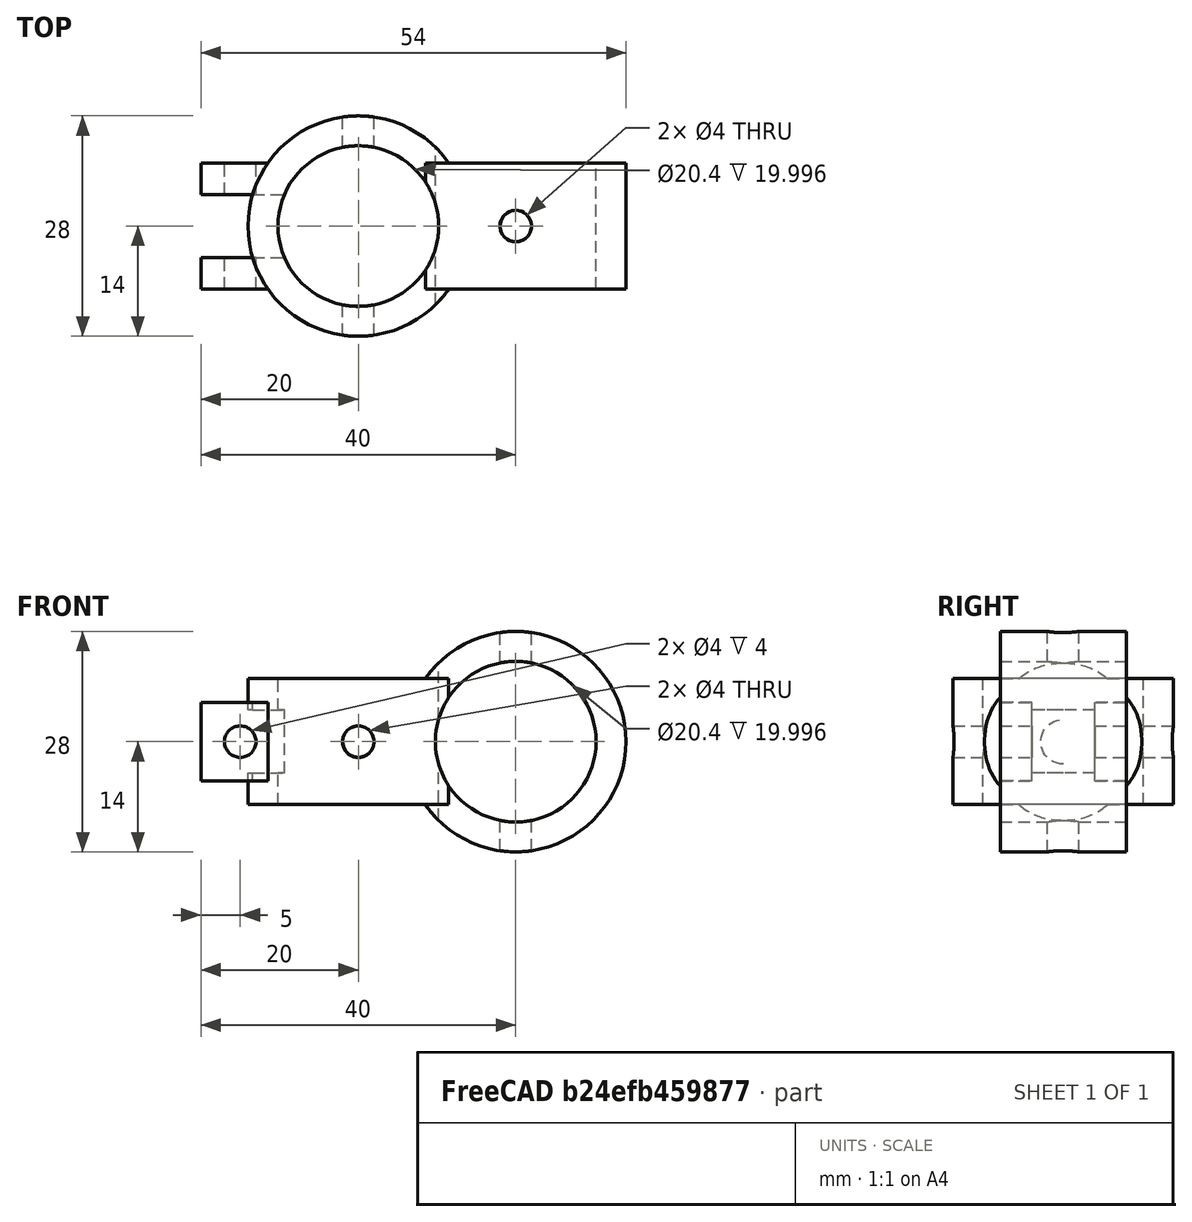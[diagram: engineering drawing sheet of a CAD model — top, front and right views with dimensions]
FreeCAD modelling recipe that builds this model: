
FCSTD DOCUMENT  (FreeCAD 0.17R13522 (Git))
Label: connector-rack-sleeper
License: All rights reserved
LicenseURL: http://en.wikipedia.org/wiki/All_rights_reserved
objects: Part::Cylinder×7, Part::Box×3, Part::MultiFuse×2, Part::Cut×1
note: 13 computed .brp shape members not serialized (recipe doc carries the construction recipe); baked Part::Feature solids carry a one-line shape summary decoded from their .brp

FEATURE [Part::Cylinder] Cylinder002
  Angle = 360
  AttacherType = Attacher::AttachEngine3D
  Height = 28
  Placement = pos=(-10,0,-10) rot=(0,0,1;0rad)
  Radius = 10.2
FEATURE [Part::Box] Box  label="Cube"
  AttacherType = Attacher::AttachEngine3D
  Height = 10
  Length = 10
  Placement = pos=(-30,-8,-5) rot=(0,0,1;0rad)
  Width = 4
FEATURE [Part::Cylinder] Cylinder004
  Angle = 360
  AttacherType = Attacher::AttachEngine3D
  Height = 16
  Placement = pos=(-25,-8,0) rot=(-1,0,0;1.5708rad)
  Radius = 2
FEATURE [Part::Cylinder] Cylinder
  Angle = 360
  AttacherType = Attacher::AttachEngine3D
  Height = 16
  Placement = pos=(-10,0,-8) rot=(0,0,1;0rad)
  Radius = 14
FEATURE [Part::Box] Box001  label="Cube001"
  AttacherType = Attacher::AttachEngine3D
  Height = 8
  Length = 5
  Placement = pos=(-24,-4,-4) rot=(0,0,1;0rad)
  Width = 8
FEATURE [Part::Cylinder] Cylinder006
  Angle = 360
  AttacherType = Attacher::AttachEngine3D
  Height = 30
  Placement = pos=(-10,-15,0) rot=(-1,0,0;1.5708rad)
  Radius = 2
FEATURE [Part::Box] Box002  label="Cube002"
  AttacherType = Attacher::AttachEngine3D
  Height = 10
  Length = 10
  Placement = pos=(-30,4,-5) rot=(0,0,1;0rad)
  Width = 4
FEATURE [Part::Cylinder] Cylinder001
  Angle = 360
  AttacherType = Attacher::AttachEngine3D
  Height = 16
  Placement = pos=(10,-8,0) rot=(-1,0,0;1.5708rad)
  Radius = 14
FEATURE [Part::MultiFuse] Fusion  label="Positive Fusion"
  Shapes = -> [Cylinder,Box,Box002,Cylinder001]
FEATURE [Part::Cylinder] Cylinder003
  Angle = 360
  AttacherType = Attacher::AttachEngine3D
  Height = 20
  Placement = pos=(10,-10,0) rot=(-1,0,0;1.5708rad)
  Radius = 10.2
FEATURE [Part::Cylinder] Cylinder005
  Angle = 360
  AttacherType = Attacher::AttachEngine3D
  Height = 30
  Placement = pos=(10,0,-15) rot=(0,0,1;0rad)
  Radius = 2
FEATURE [Part::MultiFuse] Fusion001  label="Negative Fusion"
  Shapes = -> [Cylinder002,Cylinder004,Box001,Cylinder006,Cylinder003,Cylinder005]
FEATURE [Part::Cut] Cut
  Base = -> Fusion
  Tool = -> Fusion001
